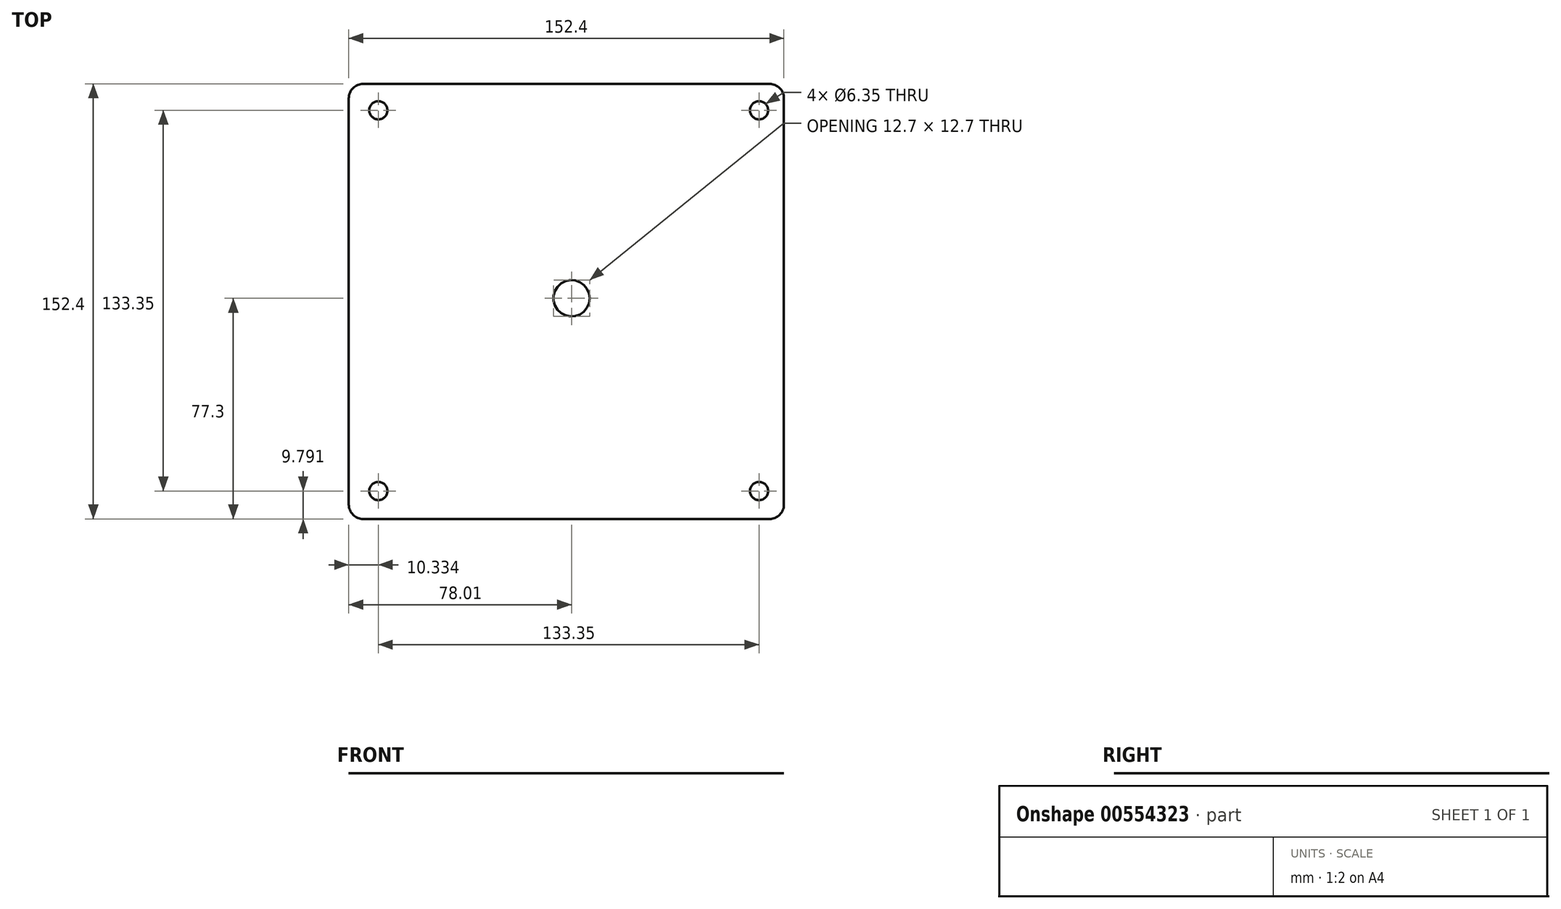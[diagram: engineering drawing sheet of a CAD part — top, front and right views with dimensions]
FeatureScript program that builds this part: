
annotation { "Feature Type Name" : "Feature", "Feature Type Description" : "" }
export const myFeature = defineFeature(function(context is Context, id is Id, definition is map)
    precondition{}
    {
        {
            var Q0;
            Q0=qCreatedBy(makeId("Top.planeOp"),FACE);
            var sketch = newSketch(context, id + "F0", { "sketchPlane" : qUnion([Q0])});
            skLineSegment(sketch, "E0.bottom", {"start": v(74.39, 75.1) * mm, "end": v(-78.01, 75.1) * mm});
            skLineSegment(sketch, "E0.top", {"start": v(74.39, -77.3) * mm, "end": v(-78.01, -77.3) * mm});
            skLineSegment(sketch, "E0.left", {"start": v(74.39, 75.1) * mm, "end": v(74.39, -77.3) * mm});
            skLineSegment(sketch, "E0.right", {"start": v(-78.01, 75.1) * mm, "end": v(-78.01, -77.3) * mm});
            skCircle(sketch, "E1", {"center": v(0, 0) * mm, "radius": 6.35 * mm});
            skCircle(sketch, "E2", {"center": v(-67.68, 65.84) * mm, "radius": 3.18 * mm});
            skCircle(sketch, "E3", {"center": v(65.67, 65.84) * mm, "radius": 3.18 * mm});
            skCircle(sketch, "E4", {"center": v(65.67, -67.5) * mm, "radius": 3.18 * mm});
            skCircle(sketch, "E5", {"center": v(-67.68, -67.5) * mm, "radius": 3.18 * mm});
            skSolve(sketch);
        }
        {
            var Q0;
            Q0=makeQuery(id+"F0.imprint","IMPRINT",FACE,{"disambiguationData":[TD([[makeQuery(id+"F0.imprint","IMPRINT",EDGE,{"derivedFrom":sQuery(id+"F0.wireOp",EDGE,"E0.bottom")}),1.0]])]});
            extrude(context, id + "F1", {"entities" : qUnion([Q0]), "depth" : 1 / 203.2 * mm, "offsetDistance" : 25.4 * mm});
        }
        {
            var Q0;
            Q0=makeQuery(id+"F1.opExtrude","SWEPT_EDGE",EDGE,{"disambiguationData":[OSD([sQuery(id+"F0.wireOp",EDGE,"E0.bottom"),sQuery(id+"F0.wireOp",EDGE,"E0.left")])]});
            var Q1;
            Q1=makeQuery(id+"F1.opExtrude","SWEPT_EDGE",EDGE,{"disambiguationData":[OSD([sQuery(id+"F0.wireOp",EDGE,"E0.bottom"),sQuery(id+"F0.wireOp",EDGE,"E0.right")])]});
            var Q2;
            Q2=makeQuery(id+"F1.opExtrude","SWEPT_EDGE",EDGE,{"disambiguationData":[OSD([sQuery(id+"F0.wireOp",EDGE,"E0.top"),sQuery(id+"F0.wireOp",EDGE,"E0.left")])]});
            var Q3;
            Q3=makeQuery(id+"F1.opExtrude","SWEPT_EDGE",EDGE,{"disambiguationData":[OSD([sQuery(id+"F0.wireOp",EDGE,"E0.top"),sQuery(id+"F0.wireOp",EDGE,"E0.right")])]});
            fillet(context, id + "F2", {"entities" : qUnion([Q0, Q1, Q2, Q3]), "radius" : 5.08 * mm, "tangentPropagation" : true, "allowEdgeOverflow" : false});
        }
        {
            var Q0;
            Q0=makeQuery(id+"F1.opExtrude","CAP_FACE",FACE,{"disambiguationData":[OSD([sQuery(id+"F0.wireOp",EDGE,"E0.bottom"),sQuery(id+"F0.wireOp",EDGE,"E0.top"),sQuery(id+"F0.wireOp",EDGE,"E0.left"),sQuery(id+"F0.wireOp",EDGE,"E0.right"),sQuery(id+"F0.wireOp",EDGE,"E1"),sQuery(id+"F0.wireOp",EDGE,"E2"),sQuery(id+"F0.wireOp",EDGE,"E3"),sQuery(id+"F0.wireOp",EDGE,"E4"),sQuery(id+"F0.wireOp",EDGE,"E5")])],"isStart":false});
            var sketch = newSketch(context, id + "F3", { "sketchPlane" : qUnion([Q0])});
            skCircle(sketch, "E6", {"center": v(0, 0) * mm, "radius": 19.04 * mm});
            skSolve(sketch);
        }
        {
            var Q0;
            Q0=makeQuery(id+"F3.imprint","IMPRINT",FACE,{"disambiguationData":[TD([[makeQuery(id+"F3.imprint","IMPRINT",EDGE,{"derivedFrom":sQuery(id+"F3.wireOp",EDGE,"E6")}),1.0]])]});
            var Q1;
            Q1=sQuery(id+"F3.wireOp",EDGE,"E6");
            extrude(context, id + "F4", {"entities" : qUnion([Q0]), "operationType" : NewBodyOperationType.REMOVE, "surfaceEntities" : qUnion([Q1]), "oppositeDirection" : true, "depth" : 1 / 914.4 * mm, "offsetDistance" : 25.4 * mm});
        }
    });
